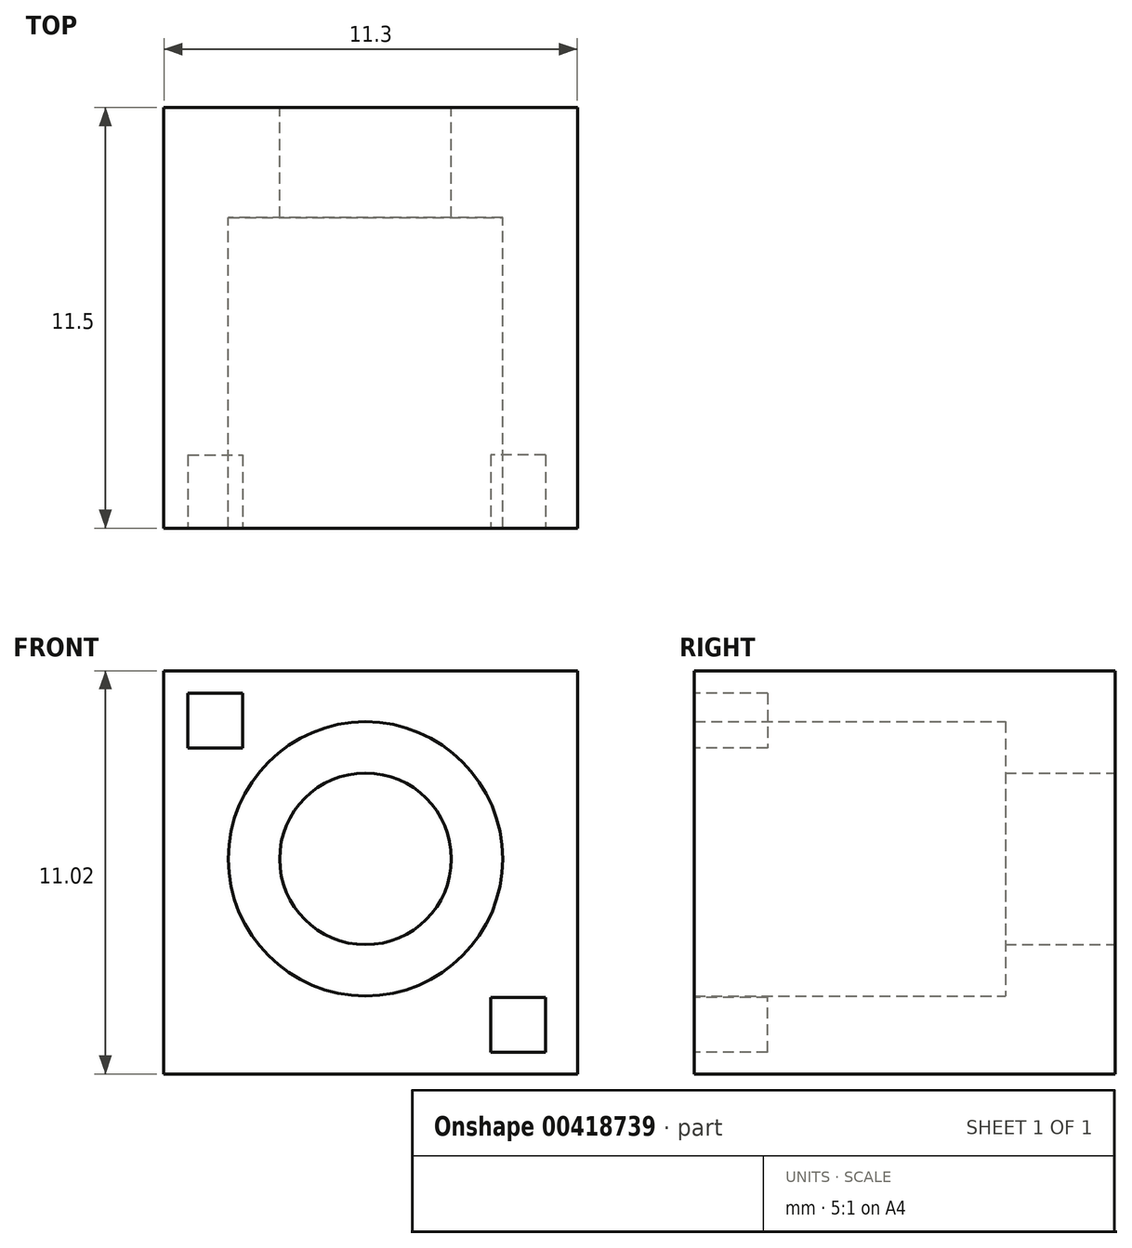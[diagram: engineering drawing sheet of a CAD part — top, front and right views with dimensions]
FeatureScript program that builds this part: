
annotation { "Feature Type Name" : "Feature", "Feature Type Description" : "" }
export const myFeature = defineFeature(function(context is Context, id is Id, definition is map)
    precondition{}
    {
        {
            var Q0;
            Q0=qCreatedBy(makeId("Front.planeOp"),FACE);
            var sketch = newSketch(context, id + "F0", { "sketchPlane" : qUnion([Q0])});
            skLineSegment(sketch, "E0.bottom", {"start": v(-9.43, 5.14) * mm, "end": v(5.8, 5.14) * mm});
            skLineSegment(sketch, "E0.top", {"start": v(-9.43, -49.22) * mm, "end": v(5.8, -49.22) * mm});
            skLineSegment(sketch, "E0.left", {"start": v(-9.43, 5.14) * mm, "end": v(-9.43, -49.22) * mm});
            skLineSegment(sketch, "E0.right", {"start": v(5.8, 5.14) * mm, "end": v(5.8, -49.22) * mm});
            skSolve(sketch);
        }
        {
            var Q0;
            Q0 = qSketchRegion(id + "F0", true);
            extrude(context, id + "F1", {"entities" : qUnion([Q0]), "depth" : 11.5 * mm});
        }
        {
            var Q0;
            Q0=qCreatedBy(makeId("Front.planeOp"),FACE);
            var sketch = newSketch(context, id + "F2", { "sketchPlane" : qUnion([Q0])});
            skCircle(sketch, "E1", {"center": v(0, 0) * mm, "radius": 3.25 * mm});
            skSolve(sketch);
        }
        {
            var Q0;
            Q0=sQuery(id+"F2.wireOp",VERTEX,"E1.center");
            var Q1;
            Q1=makeQuery(id+"F1.opExtrude","SWEPT_BODY",BODY,{"disambiguationData":[OSD([sQuery(id+"F0.wireOp",EDGE,"E0.bottom"),sQuery(id+"F0.wireOp",EDGE,"E0.top"),sQuery(id+"F0.wireOp",EDGE,"E0.left"),sQuery(id+"F0.wireOp",EDGE,"E0.right")])]});
            hole(context, id + "F3", {"style" : HoleStyle.SIMPLE, "endStyle" : HoleEndStyle.THROUGH, "oppositeDirection" : true, "holeDiameter" : 7.5 * mm, "isTappedThrough" : true, "tappedDepth" : 12 * mm, "tapClearance" : 3, "locations" : qUnion([Q0]), "scope" : qUnion([Q1])});
        }
        {
            var Q0;
            Q0=qCreatedBy(makeId("Front.planeOp"),FACE);
            var sketch = newSketch(context, id + "F4", { "sketchPlane" : qUnion([Q0])});
            skLineSegment(sketch, "E2.bottom", {"start": v(-21.08, -5.88) * mm, "end": v(21.12, -5.88) * mm});
            skLineSegment(sketch, "E2.top", {"start": v(-21.08, -50.93) * mm, "end": v(21.12, -50.93) * mm});
            skLineSegment(sketch, "E2.left", {"start": v(-21.08, -5.88) * mm, "end": v(-21.08, -50.93) * mm});
            skLineSegment(sketch, "E2.right", {"start": v(21.12, -5.88) * mm, "end": v(21.12, -50.93) * mm});
            skSolve(sketch);
        }
        {
            var Q0;
            Q0 = qSketchRegion(id + "F4", true);
            extrude(context, id + "F5", {"entities" : qUnion([Q0]), "operationType" : NewBodyOperationType.REMOVE, "depth" : 25 * mm});
        }
        {
            var Q0;
            Q0=makeQuery(id+"F1.opExtrude","CAP_FACE",FACE,{"disambiguationData":[OSD([sQuery(id+"F0.wireOp",EDGE,"E0.bottom"),sQuery(id+"F0.wireOp",EDGE,"E0.top"),sQuery(id+"F0.wireOp",EDGE,"E0.left"),sQuery(id+"F0.wireOp",EDGE,"E0.right")])],"isStart":false});
            var sketch = newSketch(context, id + "F6", { "sketchPlane" : qUnion([Q0])});
            skLineSegment(sketch, "E3.bottom", {"start": v(-5.51, -8.56) * mm, "end": v(-12, -8.56) * mm});
            skLineSegment(sketch, "E3.top", {"start": v(-5.51, 7.16) * mm, "end": v(-12, 7.16) * mm});
            skLineSegment(sketch, "E3.left", {"start": v(-5.51, -8.56) * mm, "end": v(-5.51, 7.16) * mm});
            skLineSegment(sketch, "E3.right", {"start": v(-12, -8.56) * mm, "end": v(-12, 7.16) * mm});
            skSolve(sketch);
        }
        {
            var Q0;
            Q0 = qSketchRegion(id + "F6", true);
            extrude(context, id + "F7", {"entities" : qUnion([Q0]), "operationType" : NewBodyOperationType.REMOVE, "oppositeDirection" : true, "depth" : 14 * mm});
        }
        {
            var Q0;
            Q0=makeQuery(id+"F1.opExtrude","CAP_FACE",FACE,{"disambiguationData":[OSD([sQuery(id+"F0.wireOp",EDGE,"E0.bottom"),sQuery(id+"F0.wireOp",EDGE,"E0.top"),sQuery(id+"F0.wireOp",EDGE,"E0.left"),sQuery(id+"F0.wireOp",EDGE,"E0.right")])],"isStart":true});
            var sketch = newSketch(context, id + "F8", { "sketchPlane" : qUnion([Q0])});
            skCircle(sketch, "E4", {"center": v(0, 0) * mm, "radius": 2.35 * mm});
            skCircle(sketch, "E5", {"center": v(0, 0) * mm, "radius": 4.53 * mm});
            skSolve(sketch);
        }
        {
            var Q0;
            Q0 = qSketchRegion(id + "F8", true);
            extrude(context, id + "F9", {"entities" : qUnion([Q0]), "operationType" : NewBodyOperationType.ADD, "oppositeDirection" : true, "depth" : 3 * mm});
        }
        {
            var Q0;
            Q0=makeQuery(id+"F1.opExtrude","CAP_FACE",FACE,{"disambiguationData":[OSD([sQuery(id+"F0.wireOp",EDGE,"E0.bottom"),sQuery(id+"F0.wireOp",EDGE,"E0.top"),sQuery(id+"F0.wireOp",EDGE,"E0.left"),sQuery(id+"F0.wireOp",EDGE,"E0.right")])],"isStart":false});
            var sketch = newSketch(context, id + "F10", { "sketchPlane" : qUnion([Q0])});
            skLineSegment(sketch, "E6.bottom", {"start": v(-4.85, 4.53) * mm, "end": v(-3.35, 4.53) * mm});
            skLineSegment(sketch, "E6.top", {"start": v(-4.85, 3.03) * mm, "end": v(-3.35, 3.03) * mm});
            skLineSegment(sketch, "E6.left", {"start": v(-4.85, 4.53) * mm, "end": v(-4.85, 3.03) * mm});
            skLineSegment(sketch, "E6.right", {"start": v(-3.35, 4.53) * mm, "end": v(-3.35, 3.03) * mm});
            skLineSegment(sketch, "E7.bottom", {"start": v(4.92, -5.28) * mm, "end": v(3.42, -5.28) * mm});
            skLineSegment(sketch, "E7.top", {"start": v(4.92, -3.78) * mm, "end": v(3.42, -3.78) * mm});
            skLineSegment(sketch, "E7.left", {"start": v(4.92, -5.28) * mm, "end": v(4.92, -3.78) * mm});
            skLineSegment(sketch, "E7.right", {"start": v(3.42, -5.28) * mm, "end": v(3.42, -3.78) * mm});
            skSolve(sketch);
        }
        {
            var Q0;
            Q0 = qSketchRegion(id + "F10", true);
            extrude(context, id + "F11", {"entities" : qUnion([Q0]), "operationType" : NewBodyOperationType.REMOVE, "oppositeDirection" : true, "depth" : 2 * mm});
        }
    });
